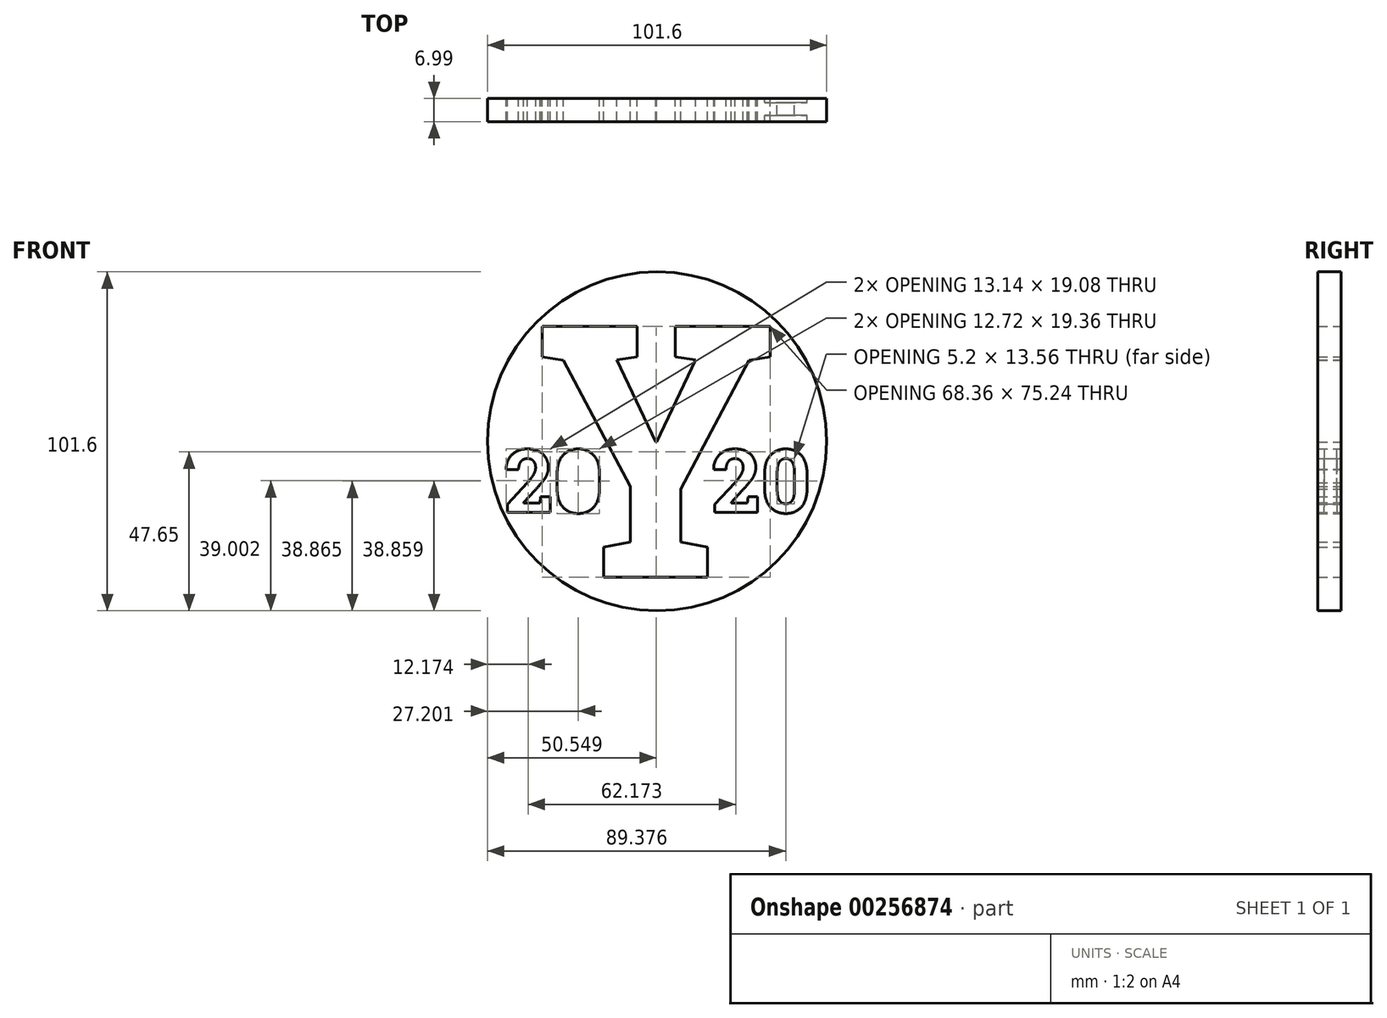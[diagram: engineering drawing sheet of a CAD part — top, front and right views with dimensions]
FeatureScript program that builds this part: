
annotation { "Feature Type Name" : "Feature", "Feature Type Description" : "" }
export const myFeature = defineFeature(function(context is Context, id is Id, definition is map)
    precondition{}
    {
        {
            var Q0;
            Q0=qCreatedBy(makeId("Front.planeOp"),FACE);
            var sketch = newSketch(context, id + "F0", { "sketchPlane" : qUnion([Q0])});
            skCircle(sketch, "E0", {"center": v(0, 0) * mm, "radius": 50.8 * mm});
            skText(sketch, "E1", { "text": "Y", "fontName": "RobotoSlab-Bold.ttf"});
            skText(sketch, "E2", { "text": "20     20", "fontName": "RobotoSlab-Bold.ttf"});
            const initialGuessF0  = {"E1": [-0.0363, -0.04077, 1, 0, 0.0762], "E2": [-0.04584, -0.02134, 1, 0, 0.01905]};
            skSetInitialGuess(sketch, initialGuessF0);
            skSolve(sketch);
        }
        {
            var Q0;
            Q0=makeQuery(id+"F0.imprint","IMPRINT",FACE,{"disambiguationData":[TD([[makeQuery(id+"F0.imprint","IMPRINT",EDGE,{"derivedFrom":sQuery(id+"F0.wireOp",EDGE,"E2.sketch_text.stroke-66")}),-1.0]])]});
            extrude(context, id + "F1", {"entities" : qUnion([Q0]), "endBound" : BoundingType.SYMMETRIC, "depth" : 3.8 * mm});
        }
        {
            var Q0;
            Q0=qSketchRegion(id+"F0",true);
            extrude(context, id + "F2", {"entities" : qUnion([Q0]), "operationType" : NewBodyOperationType.ADD, "endBound" : BoundingType.SYMMETRIC, "depth" : 6.35 * mm});
        }
        {
            var Q0;
            Q0=qSketchRegion(id+"F0",true);
            extrude(context, id + "F3", {"entities" : qUnion([Q0]), "operationType" : NewBodyOperationType.ADD, "depth" : 3.8 * mm});
        }
    });
